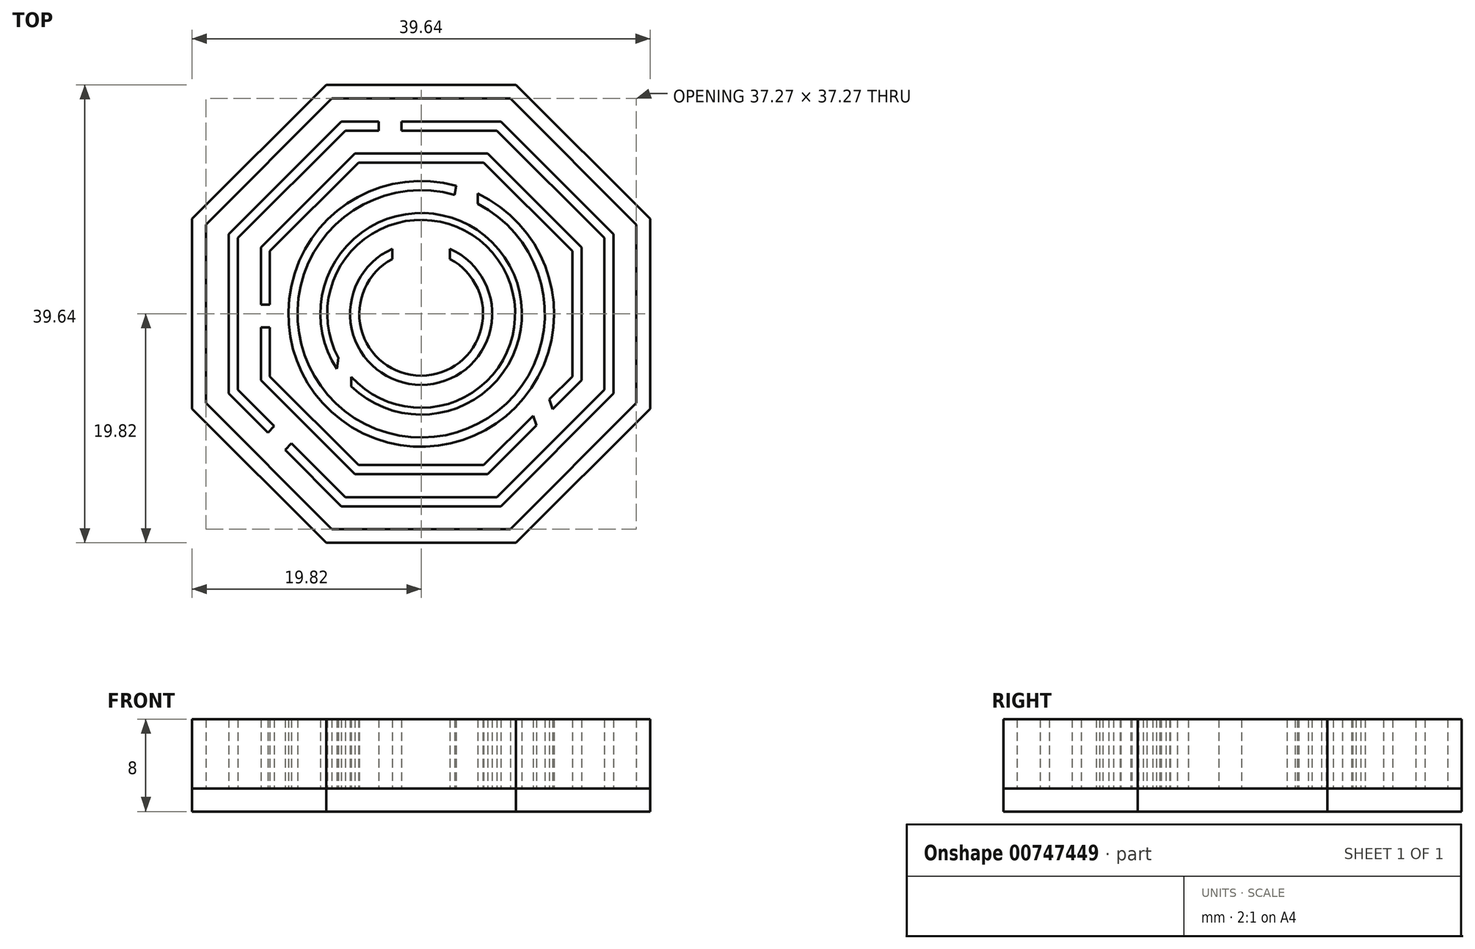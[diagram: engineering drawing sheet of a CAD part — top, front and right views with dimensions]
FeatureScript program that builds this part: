
annotation { "Feature Type Name" : "Feature", "Feature Type Description" : "" }
export const myFeature = defineFeature(function(context is Context, id is Id, definition is map)
    precondition{}
    {
        {
            var Q0;
            Q0=qCreatedBy(makeId("Top.planeOp"),FACE);
            var sketch = newSketch(context, id + "F0", { "sketchPlane" : qUnion([Q0])});
            skLineSegment(sketch, "E0.0", {"start": v(-8.21, 19.82) * mm, "end": v(8.21, 19.82) * mm});
            skLineSegment(sketch, "E0.1", {"start": v(8.21, 19.82) * mm, "end": v(19.82, 8.21) * mm});
            skLineSegment(sketch, "E0.2", {"start": v(19.82, 8.21) * mm, "end": v(19.82, -8.21) * mm});
            skLineSegment(sketch, "E0.3", {"start": v(19.82, -8.21) * mm, "end": v(8.21, -19.82) * mm});
            skLineSegment(sketch, "E0.4", {"start": v(8.21, -19.82) * mm, "end": v(-8.21, -19.82) * mm});
            skLineSegment(sketch, "E0.5", {"start": v(-8.21, -19.82) * mm, "end": v(-19.82, -8.21) * mm});
            skLineSegment(sketch, "E0.6", {"start": v(-19.82, -8.21) * mm, "end": v(-19.82, 8.21) * mm});
            skLineSegment(sketch, "E0.7", {"start": v(-19.82, 8.21) * mm, "end": v(-8.21, 19.82) * mm});
            skPoint(sketch, "E0.0.midPoint", {"position": v(0, 19.82) * mm});
            skLineSegment(sketch, "E1.0", {"start": v(-18.63, 7.72) * mm, "end": v(-7.72, 18.63) * mm});
            skLineSegment(sketch, "E1.1", {"start": v(-18.63, -7.72) * mm, "end": v(-18.63, 7.72) * mm});
            skLineSegment(sketch, "E1.2", {"start": v(-7.72, 18.63) * mm, "end": v(7.72, 18.63) * mm});
            skLineSegment(sketch, "E1.3", {"start": v(-7.72, -18.63) * mm, "end": v(-18.63, -7.72) * mm});
            skLineSegment(sketch, "E1.4", {"start": v(7.72, 18.63) * mm, "end": v(18.63, 7.72) * mm});
            skLineSegment(sketch, "E1.5", {"start": v(18.63, 7.72) * mm, "end": v(18.63, -7.72) * mm});
            skLineSegment(sketch, "E1.6", {"start": v(18.63, -7.72) * mm, "end": v(7.72, -18.63) * mm});
            skLineSegment(sketch, "E1.7", {"start": v(7.72, -18.63) * mm, "end": v(-7.72, -18.63) * mm});
            skLineSegment(sketch, "E2.0", {"start": v(-16.65, -6.9) * mm, "end": v(-16.65, 6.9) * mm});
            skLineSegment(sketch, "E2.1", {"start": v(-6.9, -16.65) * mm, "end": v(-11.77, -11.77) * mm});
            skLineSegment(sketch, "E2.2", {"start": v(-16.65, 6.9) * mm, "end": v(-6.9, 16.65) * mm});
            skLineSegment(sketch, "E2.3", {"start": v(6.9, -16.65) * mm, "end": v(-6.9, -16.65) * mm});
            skLineSegment(sketch, "E2.4", {"start": v(-6.9, 16.65) * mm, "end": v(-3.68, 16.65) * mm});
            skLineSegment(sketch, "E2.5", {"start": v(6.9, 16.65) * mm, "end": v(16.65, 6.9) * mm});
            skLineSegment(sketch, "E2.6", {"start": v(16.65, 6.9) * mm, "end": v(16.65, -6.9) * mm});
            skLineSegment(sketch, "E2.7", {"start": v(16.65, -6.9) * mm, "end": v(6.9, -16.65) * mm});
            skLineSegment(sketch, "E3.0", {"start": v(-15.86, -6.57) * mm, "end": v(-15.86, 6.57) * mm});
            skLineSegment(sketch, "E3.1", {"start": v(-6.57, -15.86) * mm, "end": v(-11.21, -11.21) * mm});
            skLineSegment(sketch, "E3.2", {"start": v(-15.86, 6.57) * mm, "end": v(-6.57, 15.86) * mm});
            skLineSegment(sketch, "E3.3", {"start": v(6.57, -15.86) * mm, "end": v(-6.57, -15.86) * mm});
            skLineSegment(sketch, "E3.4", {"start": v(-6.57, 15.86) * mm, "end": v(-3.68, 15.86) * mm});
            skLineSegment(sketch, "E3.5", {"start": v(6.57, 15.86) * mm, "end": v(15.86, 6.57) * mm});
            skLineSegment(sketch, "E3.6", {"start": v(15.86, 6.57) * mm, "end": v(15.86, -6.57) * mm});
            skLineSegment(sketch, "E3.7", {"start": v(15.86, -6.57) * mm, "end": v(6.57, -15.86) * mm});
            skLineSegment(sketch, "E4.0", {"start": v(-13.88, 5.75) * mm, "end": v(-5.75, 13.88) * mm});
            skLineSegment(sketch, "E4.1", {"start": v(-13.88, -5.75) * mm, "end": v(-13.88, -1.18) * mm});
            skLineSegment(sketch, "E4.2", {"start": v(-5.75, 13.88) * mm, "end": v(5.75, 13.88) * mm});
            skLineSegment(sketch, "E4.3", {"start": v(-5.75, -13.88) * mm, "end": v(-13.88, -5.75) * mm});
            skLineSegment(sketch, "E4.4", {"start": v(5.75, 13.88) * mm, "end": v(13.88, 5.75) * mm});
            skLineSegment(sketch, "E4.5", {"start": v(13.88, 5.75) * mm, "end": v(13.88, -5.75) * mm});
            skLineSegment(sketch, "E4.6", {"start": v(13.88, -5.75) * mm, "end": v(11.37, -8.25) * mm});
            skLineSegment(sketch, "E4.7", {"start": v(5.75, -13.88) * mm, "end": v(-5.75, -13.88) * mm});
            skLineSegment(sketch, "E5.0", {"start": v(-13.08, 5.42) * mm, "end": v(-5.42, 13.08) * mm});
            skLineSegment(sketch, "E5.1", {"start": v(-13.08, -5.42) * mm, "end": v(-13.08, -1.18) * mm});
            skLineSegment(sketch, "E5.2", {"start": v(-5.42, 13.08) * mm, "end": v(5.42, 13.08) * mm});
            skLineSegment(sketch, "E5.3", {"start": v(-5.42, -13.08) * mm, "end": v(-13.08, -5.42) * mm});
            skLineSegment(sketch, "E5.4", {"start": v(5.42, 13.08) * mm, "end": v(13.08, 5.42) * mm});
            skLineSegment(sketch, "E5.5", {"start": v(13.08, 5.42) * mm, "end": v(13.08, -5.42) * mm});
            skLineSegment(sketch, "E5.6", {"start": v(13.08, -5.42) * mm, "end": v(11.1, -7.4) * mm});
            skLineSegment(sketch, "E5.7", {"start": v(5.42, -13.08) * mm, "end": v(-5.42, -13.08) * mm});
            skArc(sketch, "E6.0", {"start": v(3.03, 11.1) * mm, "mid": v(-3.97, -10.79) * mm, "end": v(4.9, 10.4) * mm});
            skArc(sketch, "E7.0", {"start": v(2.91, 10.3) * mm, "mid": v(-3.91, -9.96) * mm, "end": v(4.9, 9.52) * mm});
            skArc(sketch, "E8.0", {"start": v(-6.04, -6.3) * mm, "mid": v(6.72, 5.57) * mm, "end": v(-7.3, -4.77) * mm});
            skArc(sketch, "E9.0", {"start": v(-6.04, -5.45) * mm, "mid": v(6.66, 4.67) * mm, "end": v(-7.17, -3.82) * mm});
            skArc(sketch, "E10.0", {"start": v(-2.5, 5.62) * mm, "mid": v(0, -6.15) * mm, "end": v(2.5, 5.62) * mm});
            skArc(sketch, "E11.0", {"start": v(-2.5, 4.74) * mm, "mid": v(0, -5.36) * mm, "end": v(2.5, 4.74) * mm});
            skLineSegment(sketch, "E12", {"start": v(-1.7, 15.86) * mm, "end": v(6.57, 15.86) * mm});
            skLineSegment(sketch, "E13", {"start": v(-1.7, 16.65) * mm, "end": v(6.9, 16.65) * mm});
            skLineSegment(sketch, "E14", {"start": v(-3.68, 16.65) * mm, "end": v(-3.68, 15.86) * mm});
            skLineSegment(sketch, "E15", {"start": v(-1.7, 16.65) * mm, "end": v(-1.7, 15.86) * mm});
            skLineSegment(sketch, "E16", {"start": v(9.7, -8.81) * mm, "end": v(5.42, -13.08) * mm});
            skLineSegment(sketch, "E17", {"start": v(9.97, -9.65) * mm, "end": v(5.75, -13.88) * mm});
            skLineSegment(sketch, "E18", {"start": v(9.7, -8.81) * mm, "end": v(9.97, -9.65) * mm});
            skLineSegment(sketch, "E19", {"start": v(11.1, -7.4) * mm, "end": v(11.37, -8.25) * mm});
            skLineSegment(sketch, "E20", {"start": v(-11.21, -11.21) * mm, "end": v(-11.77, -11.77) * mm});
            skLineSegment(sketch, "E21.trimOffspring", {"start": v(-13.27, -10.28) * mm, "end": v(-16.65, -6.9) * mm});
            skLineSegment(sketch, "E22.trimOffspring", {"start": v(-12.7, -9.72) * mm, "end": v(-15.86, -6.57) * mm});
            skLineSegment(sketch, "E23", {"start": v(-13.27, -10.28) * mm, "end": v(-12.7, -9.72) * mm});
            skLineSegment(sketch, "E24", {"start": v(-13.08, -1.18) * mm, "end": v(-13.88, -1.18) * mm});
            skLineSegment(sketch, "E25", {"start": v(-13.88, 0.8) * mm, "end": v(-13.08, 0.8) * mm});
            skLineSegment(sketch, "E26.trimOffspring", {"start": v(-13.88, 0.8) * mm, "end": v(-13.88, 5.75) * mm});
            skLineSegment(sketch, "E27.trimOffspring", {"start": v(-13.08, 0.8) * mm, "end": v(-13.08, 5.42) * mm});
            skLineSegment(sketch, "E28", {"start": v(4.9, 10.4) * mm, "end": v(4.9, 9.52) * mm});
            skLineSegment(sketch, "E29", {"start": v(2.91, 10.3) * mm, "end": v(3.03, 11.1) * mm});
            skLineSegment(sketch, "E30", {"start": v(-6.04, -6.3) * mm, "end": v(-6.04, -5.45) * mm});
            skLineSegment(sketch, "E31", {"start": v(-7.17, -3.82) * mm, "end": v(-7.3, -4.77) * mm});
            skLineSegment(sketch, "E32", {"start": v(2.5, 5.62) * mm, "end": v(2.5, 4.74) * mm});
            skLineSegment(sketch, "E33", {"start": v(-2.5, 4.74) * mm, "end": v(-2.5, 5.62) * mm});
            skSolve(sketch);
        }
        {
            var Q0;
            Q0 = qSketchRegion(id + "F0", true);
            var Q1;
            Q1=makeQuery(id+"F0.imprint","IMPRINT",FACE,{"disambiguationData":[TD([[makeQuery(id+"F0.imprint","IMPRINT",EDGE,{"derivedFrom":sQuery(id+"F0.wireOp",EDGE,"E2.0")}),-1.0]])]});
            var Q2;
            Q2=makeQuery(id+"F0.imprint","IMPRINT",FACE,{"disambiguationData":[TD([[makeQuery(id+"F0.imprint","IMPRINT",EDGE,{"derivedFrom":sQuery(id+"F0.wireOp",EDGE,"E4.0")}),-1.0]])]});
            var Q3;
            Q3=makeQuery(id+"F0.imprint","IMPRINT",FACE,{"disambiguationData":[TD([[makeQuery(id+"F0.imprint","IMPRINT",EDGE,{"derivedFrom":sQuery(id+"F0.wireOp",EDGE,"E6.0")}),1.0]])]});
            var Q4;
            Q4=makeQuery(id+"F0.imprint","IMPRINT",FACE,{"disambiguationData":[TD([[makeQuery(id+"F0.imprint","IMPRINT",EDGE,{"derivedFrom":sQuery(id+"F0.wireOp",EDGE,"E8.0")}),1.0]])]});
            var Q5;
            Q5=makeQuery(id+"F0.imprint","IMPRINT",FACE,{"disambiguationData":[TD([[makeQuery(id+"F0.imprint","IMPRINT",EDGE,{"derivedFrom":sQuery(id+"F0.wireOp",EDGE,"E10.0")}),1.0]])]});
            var Q6;
            Q6=makeQuery(id+"F0.imprint","IMPRINT",FACE,{"disambiguationData":[TD([[makeQuery(id+"F0.imprint","IMPRINT",EDGE,{"derivedFrom":sQuery(id+"F0.wireOp",EDGE,"E2.1")}),-1.0]])]});
            var Q7;
            Q7=makeQuery(id+"F0.imprint","IMPRINT",FACE,{"disambiguationData":[TD([[makeQuery(id+"F0.imprint","IMPRINT",EDGE,{"derivedFrom":sQuery(id+"F0.wireOp",EDGE,"E4.1")}),-1.0]])]});
            extrude(context, id + "F1", {"entities" : qUnion([Q0, Q1, Q2, Q3, Q4, Q5, Q6, Q7]), "depth" : 6 * mm, "offsetDistance" : 25 * mm});
        }
        {
            var Q0;
            Q0=qCreatedBy(makeId("Top.planeOp"),FACE);
            var sketch = newSketch(context, id + "F2", { "sketchPlane" : qUnion([Q0])});
            skLineSegment(sketch, "E34.0", {"start": v(19.82, -8.21) * mm, "end": v(8.21, -19.82) * mm});
            skLineSegment(sketch, "E35.0", {"start": v(8.21, -19.82) * mm, "end": v(-8.21, -19.82) * mm});
            skLineSegment(sketch, "E36.0", {"start": v(-8.21, -19.82) * mm, "end": v(-19.82, -8.21) * mm});
            skLineSegment(sketch, "E37.0", {"start": v(-19.82, -8.21) * mm, "end": v(-19.82, 8.21) * mm});
            skLineSegment(sketch, "E38.0.0", {"start": v(-8.21, 19.82) * mm, "end": v(-19.82, 8.21) * mm});
            skLineSegment(sketch, "E38.0.1", {"start": v(-19.82, 8.21) * mm, "end": v(-19.82, -8.21) * mm});
            skLineSegment(sketch, "E38.0.2", {"start": v(-19.82, -8.21) * mm, "end": v(-8.21, -19.82) * mm});
            skLineSegment(sketch, "E38.0.3", {"start": v(-8.21, -19.82) * mm, "end": v(8.21, -19.82) * mm});
            skLineSegment(sketch, "E38.0.4", {"start": v(8.21, -19.82) * mm, "end": v(19.82, -8.21) * mm});
            skLineSegment(sketch, "E38.0.5", {"start": v(19.82, -8.21) * mm, "end": v(19.82, 8.21) * mm});
            skLineSegment(sketch, "E38.0.6", {"start": v(19.82, 8.21) * mm, "end": v(8.21, 19.82) * mm});
            skLineSegment(sketch, "E38.0.7", {"start": v(8.21, 19.82) * mm, "end": v(-8.21, 19.82) * mm});
            skSolve(sketch);
        }
        {
            var Q0;
            Q0 = qSketchRegion(id + "F2", true);
            extrude(context, id + "F3", {"entities" : qUnion([Q0]), "oppositeDirection" : true, "depth" : 2 * mm, "offsetDistance" : 25 * mm});
        }
    });
